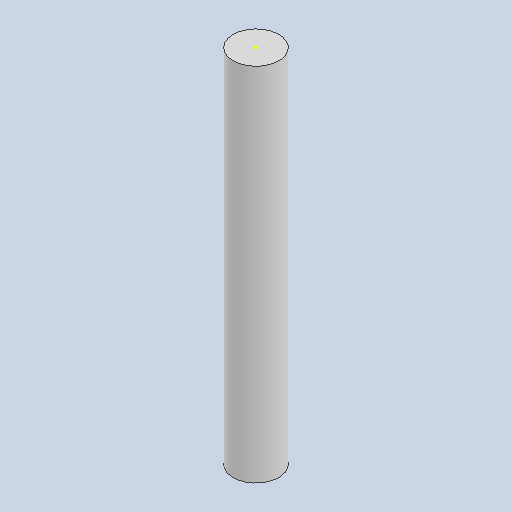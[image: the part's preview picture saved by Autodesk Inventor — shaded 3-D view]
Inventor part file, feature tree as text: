
AUTODESK INVENTOR PART (.ipt)
format: ipt  version: 2025.2 (Build 292293000, 293)  size: 244,224 bytes
history: native  units: in
note: dims shown in document units (in); Inventor stores cm internally (conversion verified against a paired STEP export)
features: sketch x2, extrude x1
ambient origin geometry x8: Origin, YZ Plane, XZ Plane, XY Plane, X Axis, Y Axis, Z Axis, Center Point
bodies: Solid1 (feature_tree)
feature tree (3):
  extrude  "Extrusion1"  Depth=0.5906in TaperAngle=0.0deg
  sketch  "Sketch2"
  sketch  "Sketch1"  dims[d0=0.0748in d1=0.5906in d2=0.0in]
